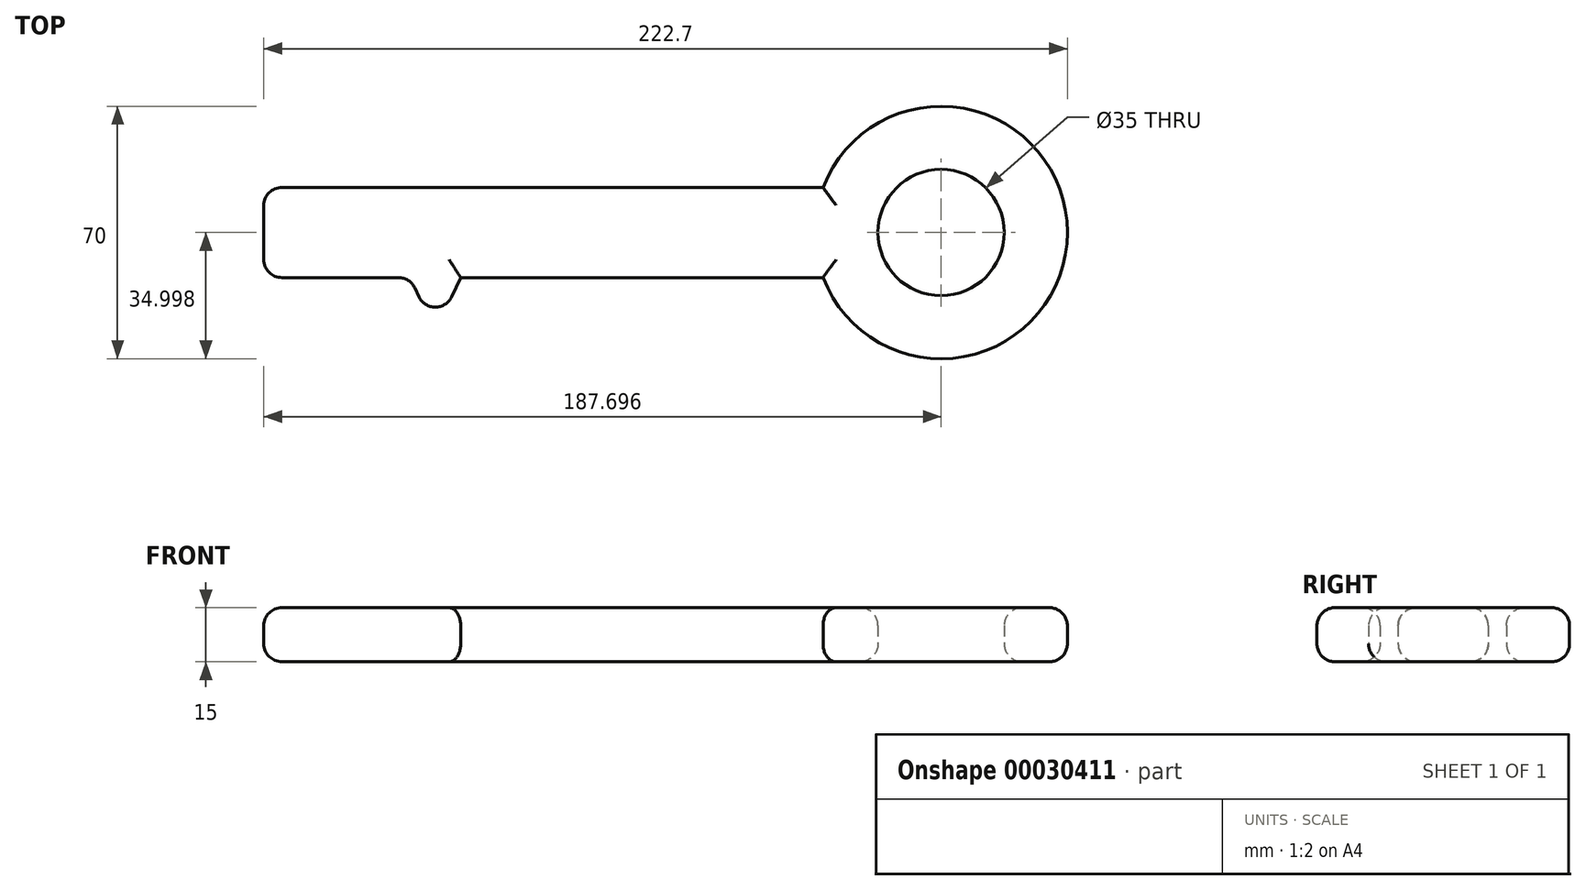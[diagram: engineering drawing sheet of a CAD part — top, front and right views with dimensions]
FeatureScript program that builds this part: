
annotation { "Feature Type Name" : "Feature", "Feature Type Description" : "" }
export const myFeature = defineFeature(function(context is Context, id is Id, definition is map)
    precondition{}
    {
        {
            var Q0;
            Q0=qCreatedBy(makeId("Top.planeOp"),FACE);
            var sketch = newSketch(context, id + "F0", { "sketchPlane" : qUnion([Q0])});
            skLineSegment(sketch, "E0.bottom", {"start": v(122.66, 39.98) * mm, "end": v(-32.34, 39.98) * mm});
            skLineSegment(sketch, "E0.top", {"start": v(122.66, 14.98) * mm, "end": v(-32.34, 14.98) * mm});
            skLineSegment(sketch, "E0.left", {"start": v(122.66, 39.98) * mm, "end": v(122.66, 14.98) * mm});
            skLineSegment(sketch, "E0.right", {"start": v(-32.34, 39.98) * mm, "end": v(-32.34, 14.98) * mm});
            skLineSegment(sketch, "E1.bottom", {"start": v(-19.83, 14.98) * mm, "end": v(-29.83, 14.98) * mm});
            skLineSegment(sketch, "E1.top", {"start": v(-19.83, -13.72) * mm, "end": v(-29.83, -13.72) * mm});
            skLineSegment(sketch, "E1.left", {"start": v(-19.83, 14.98) * mm, "end": v(-19.83, -13.72) * mm});
            skLineSegment(sketch, "E1.right", {"start": v(-29.83, 14.98) * mm, "end": v(-29.83, -13.72) * mm});
            skLineSegment(sketch, "E2.bottom", {"start": v(-9.83, 14.98) * mm, "end": v(-1.83, 14.98) * mm});
            skLineSegment(sketch, "E2.top", {"start": v(-9.83, -0.02) * mm, "end": v(-1.83, -0.02) * mm});
            skLineSegment(sketch, "E2.left", {"start": v(-9.83, 14.98) * mm, "end": v(-9.83, -0.02) * mm});
            skLineSegment(sketch, "E2.right", {"start": v(-1.83, 14.98) * mm, "end": v(-1.83, -0.02) * mm});
            skLineSegment(sketch, "E3", {"start": v(8.17, 14.98) * mm, "end": v(15.17, 0) * mm});
            skLineSegment(sketch, "E4", {"start": v(15.17, 0) * mm, "end": v(22.21, 14.98) * mm});
            skArc(sketch, "E5", {"start": v(122.66, 14.98) * mm, "mid": v(190.36, 27.48) * mm, "end": v(122.66, 39.98) * mm});
            skCircle(sketch, "E6", {"center": v(155.36, 27.48) * mm, "radius": 17.5 * mm});
            skLineSegment(sketch, "E7", {"start": v(155.36, 27.48) * mm, "end": v(-32.34, 27.48) * mm, "construction": true});
            skSolve(sketch);
        }
        {
            var Q0;
            Q0=makeQuery(id+"F0.imprint","IMPRINT",FACE,{"disambiguationData":[TD([[makeQuery(id+"F0.imprint","IMPRINT",EDGE,{"derivedFrom":sQuery(id+"F0.wireOp",EDGE,"E0.bottom")}),1.0]])]});
            var Q1;
            Q1=makeQuery(id+"F0.imprint","IMPRINT",FACE,{"disambiguationData":[TD([[makeQuery(id+"F0.imprint","IMPRINT",EDGE,{"derivedFrom":sQuery(id+"F0.wireOp",EDGE,"E0.left")}),1.0]])]});
            var Q2;
            Q2=makeQuery(id+"F0.imprint","IMPRINT",FACE,{"disambiguationData":[TD([[makeQuery(id+"F0.imprint","IMPRINT",EDGE,{"derivedFrom":sQuery(id+"F0.wireOp",EDGE,"E1.bottom")}),1.0]])]});
            var Q3;
            Q3=makeQuery(id+"F0.imprint","IMPRINT",FACE,{"disambiguationData":[TD([[makeQuery(id+"F0.imprint","IMPRINT",EDGE,{"derivedFrom":sQuery(id+"F0.wireOp",EDGE,"E2.bottom")}),-1.0]])]});
            var Q4;
            {var subQ1=sQuery(id+"F0.wireOp",EDGE,"E3");Q4=makeQuery(id+"F0.imprint","IMPRINT",FACE,{"disambiguationData":[TD([[makeQuery(id+"F0.imprint","IMPRINT",EDGE,{"derivedFrom":subQ1}),1.0]])]});}
            var Q5;
            Q5=sQuery(id+"F0.wireOp",EDGE,"E0.top");
            extrude(context, id + "F1", {"entities" : qUnion([Q0, Q1, Q2, Q3, Q4]), "surfaceEntities" : qUnion([Q5]), "depth" : 15 * mm});
        }
        {
            var Q0;
            {var subQ0=sQuery(id+"F0.wireOp",EDGE,"E0.top");Q0=makeQuery(id+"F1.opExtrude","CAP_EDGE",EDGE,{"disambiguationData":[OSD([subQ0]),TDD([makeQuery(id+"F0.imprint","IMPRINT",EDGE,{"disambiguationData":[TD([[makeQuery(id+"F0.imprint","INTERSECT",VERTEX,{"derivedFrom":[subQ0,sQuery(id+"F0.wireOp",EDGE,"E4")]}),1.0]])],"derivedFrom":subQ0})])],"isStart":false});}
            var Q1;
            Q1=makeQuery(id+"F1.opExtrude","CAP_EDGE",EDGE,{"disambiguationData":[OSD([sQuery(id+"F0.wireOp",EDGE,"E5")])],"isStart":false});
            var Q2;
            Q2=makeQuery(id+"F1.opExtrude","CAP_EDGE",EDGE,{"disambiguationData":[OSD([sQuery(id+"F0.wireOp",EDGE,"E0.bottom")])],"isStart":false});
            var Q3;
            Q3=makeQuery(id+"F1.opExtrude","CAP_EDGE",EDGE,{"disambiguationData":[OSD([sQuery(id+"F0.wireOp",EDGE,"E6")])],"isStart":false});
            var Q4;
            Q4=makeQuery(id+"F1.opExtrude","CAP_FACE",FACE,{"disambiguationData":[OSD([sQuery(id+"F0.wireOp",EDGE,"E0.bottom"),sQuery(id+"F0.wireOp",EDGE,"E0.top"),sQuery(id+"F0.wireOp",EDGE,"E0.right"),sQuery(id+"F0.wireOp",EDGE,"E1.top"),sQuery(id+"F0.wireOp",EDGE,"E1.left"),sQuery(id+"F0.wireOp",EDGE,"E1.right"),sQuery(id+"F0.wireOp",EDGE,"E2.top"),sQuery(id+"F0.wireOp",EDGE,"E2.left"),sQuery(id+"F0.wireOp",EDGE,"E2.right"),sQuery(id+"F0.wireOp",EDGE,"E3"),sQuery(id+"F0.wireOp",EDGE,"E4"),sQuery(id+"F0.wireOp",EDGE,"E5"),sQuery(id+"F0.wireOp",EDGE,"E6")])],"isStart":false});
            var Q5;
            Q5=makeQuery(id+"F1.opExtrude","CAP_EDGE",EDGE,{"disambiguationData":[OSD([sQuery(id+"F0.wireOp",EDGE,"E4")])],"isStart":false});
            var Q6;
            Q6=makeQuery(id+"F1.opExtrude","SWEPT_EDGE",EDGE,{"disambiguationData":[OSD([sQuery(id+"F0.wireOp",EDGE,"E3"),sQuery(id+"F0.wireOp",EDGE,"E4")])]});
            var Q7;
            Q7=makeQuery(id+"F1.opExtrude","CAP_EDGE",EDGE,{"disambiguationData":[OSD([sQuery(id+"F0.wireOp",EDGE,"E4")])],"isStart":true});
            var Q8;
            Q8=makeQuery(id+"F1.opExtrude","CAP_EDGE",EDGE,{"disambiguationData":[OSD([sQuery(id+"F0.wireOp",EDGE,"E2.right")])],"isStart":false});
            var Q9;
            Q9=makeQuery(id+"F1.opExtrude","CAP_EDGE",EDGE,{"disambiguationData":[OSD([sQuery(id+"F0.wireOp",EDGE,"E2.right")])],"isStart":true});
            var Q10;
            {var subQ0=sQuery(id+"F0.wireOp",EDGE,"E0.top");Q10=makeQuery(id+"F1.opExtrude","SWEPT_FACE",FACE,{"disambiguationData":[OSD([subQ0]),TDD([makeQuery(id+"F0.imprint","IMPRINT",EDGE,{"disambiguationData":[TD([[makeQuery(id+"F0.imprint","INTERSECT",VERTEX,{"derivedFrom":[subQ0,sQuery(id+"F0.wireOp",EDGE,"E3")]}),-1.0]])],"derivedFrom":subQ0})])]});}
            var Q11;
            {var subQ0=sQuery(id+"F0.wireOp",EDGE,"E0.top");Q11=makeQuery(id+"F1.opExtrude","CAP_EDGE",EDGE,{"disambiguationData":[OSD([subQ0]),TDD([makeQuery(id+"F0.imprint","IMPRINT",EDGE,{"disambiguationData":[TD([[makeQuery(id+"F0.imprint","INTERSECT",VERTEX,{"derivedFrom":[subQ0,sQuery(id+"F0.wireOp",EDGE,"E3")]}),-1.0]])],"derivedFrom":subQ0})])],"isStart":false});}
            var Q12;
            {var subQ0=sQuery(id+"F0.wireOp",EDGE,"E0.top");Q12=makeQuery(id+"F1.opExtrude","CAP_EDGE",EDGE,{"disambiguationData":[OSD([subQ0]),TDD([makeQuery(id+"F0.imprint","IMPRINT",EDGE,{"disambiguationData":[TD([[makeQuery(id+"F0.imprint","INTERSECT",VERTEX,{"derivedFrom":[subQ0,sQuery(id+"F0.wireOp",EDGE,"E1.bottom"),sQuery(id+"F0.wireOp",EDGE,"E1.left")]}),1.0]])],"derivedFrom":subQ0})])],"isStart":false});}
            var Q13;
            Q13=makeQuery(id+"F1.opExtrude","CAP_EDGE",EDGE,{"disambiguationData":[OSD([sQuery(id+"F0.wireOp",EDGE,"E2.left")])],"isStart":false});
            var Q14;
            Q14=makeQuery(id+"F1.opExtrude","CAP_EDGE",EDGE,{"disambiguationData":[OSD([sQuery(id+"F0.wireOp",EDGE,"E1.left")])],"isStart":false});
            var Q15;
            Q15=makeQuery(id+"F1.opExtrude","SWEPT_EDGE",EDGE,{"disambiguationData":[OSD([sQuery(id+"F0.wireOp",EDGE,"E1.top"),sQuery(id+"F0.wireOp",EDGE,"E1.left")])]});
            var Q16;
            Q16=makeQuery(id+"F1.opExtrude","CAP_EDGE",EDGE,{"disambiguationData":[OSD([sQuery(id+"F0.wireOp",EDGE,"E1.left")])],"isStart":true});
            var Q17;
            Q17=makeQuery(id+"F1.opExtrude","CAP_EDGE",EDGE,{"disambiguationData":[OSD([sQuery(id+"F0.wireOp",EDGE,"E1.top")])],"isStart":false});
            var Q18;
            Q18=makeQuery(id+"F1.opExtrude","CAP_EDGE",EDGE,{"disambiguationData":[OSD([sQuery(id+"F0.wireOp",EDGE,"E1.top")])],"isStart":true});
            var Q19;
            Q19=makeQuery(id+"F1.opExtrude","CAP_EDGE",EDGE,{"disambiguationData":[OSD([sQuery(id+"F0.wireOp",EDGE,"E1.right")])],"isStart":false});
            var Q20;
            {var subQ0=sQuery(id+"F0.wireOp",EDGE,"E0.top");Q20=makeQuery(id+"F1.opExtrude","CAP_EDGE",EDGE,{"disambiguationData":[OSD([subQ0]),TDD([makeQuery(id+"F0.imprint","IMPRINT",EDGE,{"disambiguationData":[TD([[makeQuery(id+"F0.imprint","INTERSECT",VERTEX,{"derivedFrom":[subQ0,sQuery(id+"F0.wireOp",EDGE,"E0.right")]}),1.0]])],"derivedFrom":subQ0})])],"isStart":false});}
            var Q21;
            Q21=makeQuery(id+"F1.opExtrude","CAP_EDGE",EDGE,{"disambiguationData":[OSD([sQuery(id+"F0.wireOp",EDGE,"E0.right")])],"isStart":false});
            var Q22;
            {var subQ0=sQuery(id+"F0.wireOp",EDGE,"E0.top");Q22=makeQuery(id+"F1.opExtrude","CAP_EDGE",EDGE,{"disambiguationData":[OSD([subQ0]),TDD([makeQuery(id+"F0.imprint","IMPRINT",EDGE,{"disambiguationData":[TD([[makeQuery(id+"F0.imprint","INTERSECT",VERTEX,{"derivedFrom":[subQ0,sQuery(id+"F0.wireOp",EDGE,"E4")]}),1.0]])],"derivedFrom":subQ0})])],"isStart":true});}
            var Q23;
            Q23=makeQuery(id+"F1.opExtrude","CAP_EDGE",EDGE,{"disambiguationData":[OSD([sQuery(id+"F0.wireOp",EDGE,"E5")])],"isStart":true});
            var Q24;
            Q24=makeQuery(id+"F1.opExtrude","SWEPT_FACE",FACE,{"disambiguationData":[OSD([sQuery(id+"F0.wireOp",EDGE,"E2.top")])]});
            var Q25;
            Q25=makeQuery(id+"F1.opExtrude","SWEPT_EDGE",EDGE,{"disambiguationData":[OSD([sQuery(id+"F0.wireOp",EDGE,"E2.top"),sQuery(id+"F0.wireOp",EDGE,"E2.left")])]});
            var Q26;
            Q26=makeQuery(id+"F1.opExtrude","SWEPT_EDGE",EDGE,{"disambiguationData":[OSD([sQuery(id+"F0.wireOp",EDGE,"E1.top"),sQuery(id+"F0.wireOp",EDGE,"E1.right")])]});
            var Q27;
            Q27=makeQuery(id+"F1.opExtrude","SWEPT_EDGE",EDGE,{"disambiguationData":[OSD([sQuery(id+"F0.wireOp",EDGE,"E0.top"),sQuery(id+"F0.wireOp",EDGE,"E0.right")])]});
            var Q28;
            {var subQ0=sQuery(id+"F0.wireOp",EDGE,"E0.top");Q28=makeQuery(id+"F1.opExtrude","CAP_EDGE",EDGE,{"disambiguationData":[OSD([subQ0]),TDD([makeQuery(id+"F0.imprint","IMPRINT",EDGE,{"disambiguationData":[TD([[makeQuery(id+"F0.imprint","INTERSECT",VERTEX,{"derivedFrom":[subQ0,sQuery(id+"F0.wireOp",EDGE,"E1.bottom"),sQuery(id+"F0.wireOp",EDGE,"E1.left")]}),1.0]])],"derivedFrom":subQ0})])],"isStart":true});}
            var Q29;
            Q29=makeQuery(id+"F1.opExtrude","CAP_EDGE",EDGE,{"disambiguationData":[OSD([sQuery(id+"F0.wireOp",EDGE,"E3")])],"isStart":true});
            var Q30;
            Q30=makeQuery(id+"F1.opExtrude","CAP_EDGE",EDGE,{"disambiguationData":[OSD([sQuery(id+"F0.wireOp",EDGE,"E0.bottom")])],"isStart":true});
            var Q31;
            Q31=makeQuery(id+"F1.opExtrude","SWEPT_EDGE",EDGE,{"disambiguationData":[OSD([sQuery(id+"F0.wireOp",EDGE,"E0.bottom"),sQuery(id+"F0.wireOp",EDGE,"E0.right")])]});
            var Q32;
            Q32=makeQuery(id+"F1.opExtrude","CAP_EDGE",EDGE,{"disambiguationData":[OSD([sQuery(id+"F0.wireOp",EDGE,"E0.right")])],"isStart":true});
            var Q33;
            Q33=makeQuery(id+"F1.opExtrude","CAP_EDGE",EDGE,{"disambiguationData":[OSD([sQuery(id+"F0.wireOp",EDGE,"E1.right")])],"isStart":true});
            var Q34;
            Q34=makeQuery(id+"F1.opExtrude","CAP_EDGE",EDGE,{"disambiguationData":[OSD([sQuery(id+"F0.wireOp",EDGE,"E6")])],"isStart":true});
            var Q35;
            Q35=makeQuery(id+"F1.opExtrude","CAP_EDGE",EDGE,{"disambiguationData":[OSD([sQuery(id+"F0.wireOp",EDGE,"E2.left")])],"isStart":true});
            var Q36;
            {var subQ0=sQuery(id+"F0.wireOp",EDGE,"E0.top");Q36=makeQuery(id+"F1.opExtrude","CAP_EDGE",EDGE,{"disambiguationData":[OSD([subQ0]),TDD([makeQuery(id+"F0.imprint","IMPRINT",EDGE,{"disambiguationData":[TD([[makeQuery(id+"F0.imprint","INTERSECT",VERTEX,{"derivedFrom":[subQ0,sQuery(id+"F0.wireOp",EDGE,"E3")]}),-1.0]])],"derivedFrom":subQ0})])],"isStart":true});}
            fillet(context, id + "F2", {"entities" : qUnion([Q0, Q1, Q2, Q3, Q4, Q5, Q6, Q7, Q8, Q9, Q10, Q11, Q12, Q13, Q14, Q15, Q16, Q17, Q18, Q19, Q20, Q21, Q22, Q23, Q24, Q25, Q26, Q27, Q28, Q29, Q30, Q31, Q32, Q33, Q34, Q35, Q36]), "radius" : 5 * mm, "tangentPropagation" : true, "allowEdgeOverflow" : false});
        }
    });
